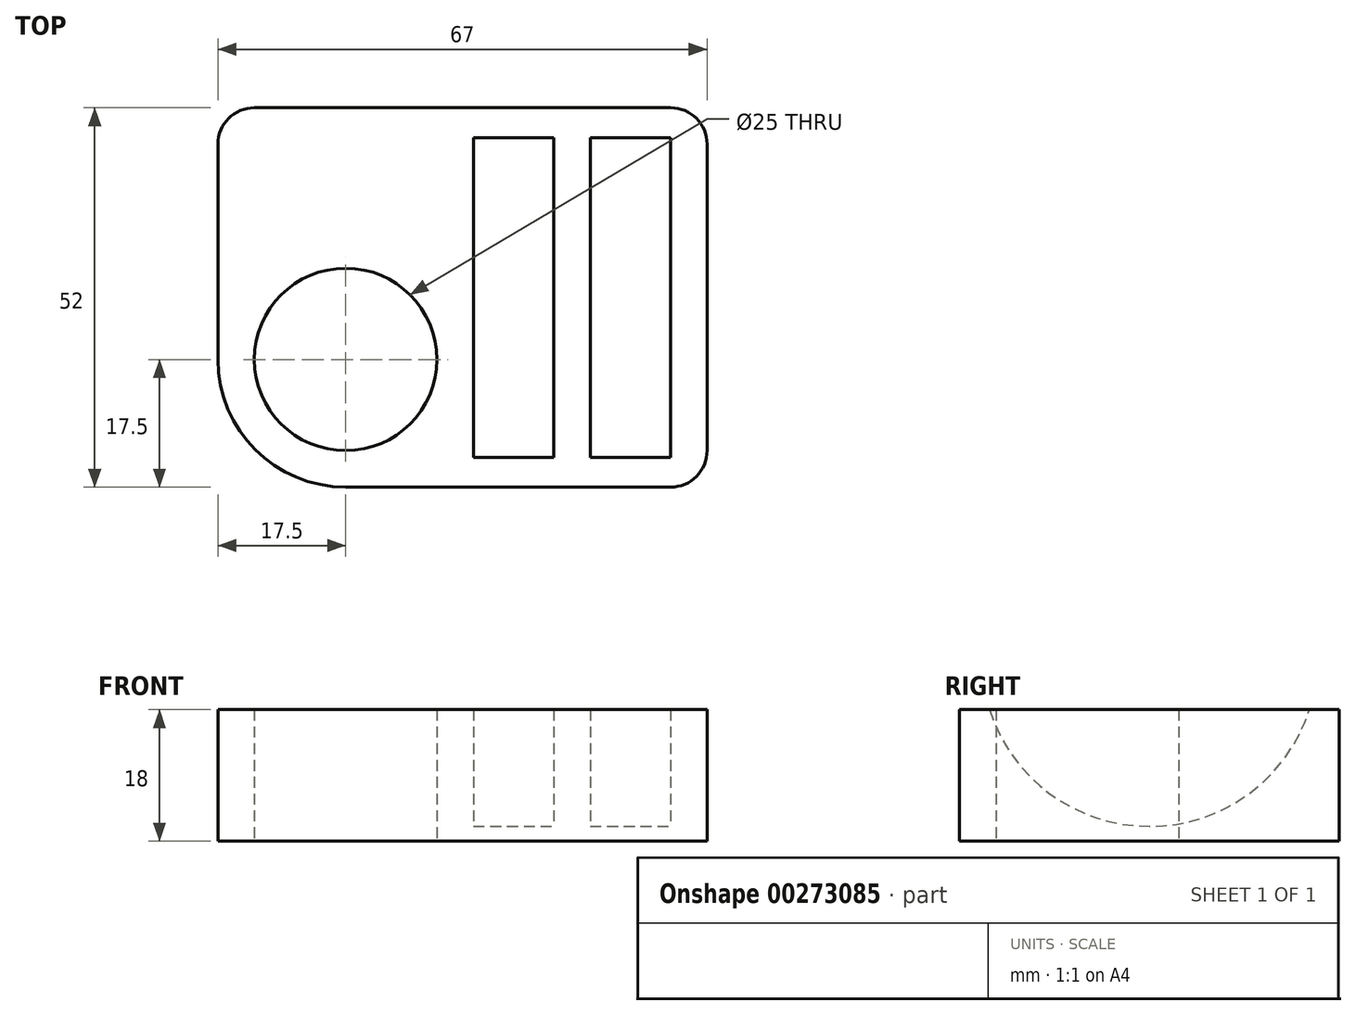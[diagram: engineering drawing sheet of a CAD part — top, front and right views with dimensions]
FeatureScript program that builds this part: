
annotation { "Feature Type Name" : "Feature", "Feature Type Description" : "" }
export const myFeature = defineFeature(function(context is Context, id is Id, definition is map)
    precondition{}
    {
        {
            var Q0;
            Q0=qCreatedBy(makeId("Top.planeOp"),FACE);
            var sketch = newSketch(context, id + "F0", { "sketchPlane" : qUnion([Q0])});
            skLineSegment(sketch, "E0.bottom", {"start": v(17.5, 0) * mm, "end": v(62, 0) * mm});
            skLineSegment(sketch, "E0.top", {"start": v(5, 52) * mm, "end": v(62, 52) * mm});
            skLineSegment(sketch, "E0.left", {"start": v(0, 17.5) * mm, "end": v(0, 47) * mm});
            skLineSegment(sketch, "E0.right", {"start": v(67, 5) * mm, "end": v(67, 47) * mm});
            skLineSegment(sketch, "E1.bottom", {"start": v(0, 0) * mm, "end": v(17.5, 0) * mm, "construction": true});
            skLineSegment(sketch, "E1.top", {"start": v(0, 17.5) * mm, "end": v(17.5, 17.5) * mm, "construction": true});
            skLineSegment(sketch, "E1.left", {"start": v(0, 0) * mm, "end": v(0, 17.5) * mm, "construction": true});
            skLineSegment(sketch, "E1.right", {"start": v(17.5, 0) * mm, "end": v(17.5, 17.5) * mm, "construction": true});
            skCircle(sketch, "E2", {"center": v(17.5, 17.5) * mm, "radius": 12.5 * mm});
            skPoint(sketch, "E3.visualSharp", {"position": v(0, 0) * mm});
            skArc(sketch, "E3.filletArc", {"start": v(0, 17.5) * mm, "mid": v(5.13, 5.13) * mm, "end": v(17.5, 0) * mm});
            skPoint(sketch, "E4.visualSharp", {"position": v(0, 52) * mm});
            skArc(sketch, "E4.filletArc", {"start": v(5, 52) * mm, "mid": v(1.46, 50.54) * mm, "end": v(0, 47) * mm});
            skPoint(sketch, "E5.visualSharp", {"position": v(67, 52) * mm});
            skArc(sketch, "E5.filletArc", {"start": v(67, 47) * mm, "mid": v(65.54, 50.54) * mm, "end": v(62, 52) * mm});
            skPoint(sketch, "E6.visualSharp", {"position": v(67, 0) * mm});
            skArc(sketch, "E6.filletArc", {"start": v(62, 0) * mm, "mid": v(65.54, 1.46) * mm, "end": v(67, 5) * mm});
            skSolve(sketch);
        }
        {
            var Q0;
            Q0=makeQuery(id+"F0.imprint","IMPRINT",FACE,{"disambiguationData":[TD([[makeQuery(id+"F0.imprint","IMPRINT",EDGE,{"derivedFrom":sQuery(id+"F0.wireOp",EDGE,"E0.bottom")}),1.0]])]});
            extrude(context, id + "F1", {"entities" : qUnion([Q0]), "depth" : 25 * mm});
        }
        {
            var Q0;
            Q0=makeQuery(id+"F1.opExtrude","CAP_FACE",FACE,{"disambiguationData":[OSD([sQuery(id+"F0.wireOp",EDGE,"E0.bottom"),sQuery(id+"F0.wireOp",EDGE,"E0.top"),sQuery(id+"F0.wireOp",EDGE,"E0.right"),sQuery(id+"F0.wireOp",EDGE,"E2"),sQuery(id+"F0.wireOp",EDGE,"E3.filletArc"),sQuery(id+"F0.wireOp",EDGE,"E4.filletArc"),sQuery(id+"F0.wireOp",EDGE,"E5.filletArc"),sQuery(id+"F0.wireOp",EDGE,"E6.filletArc")])],"isStart":false});
            var sketch = newSketch(context, id + "F2", { "sketchPlane" : qUnion([Q0])});
            skLineSegment(sketch, "E7.bottom", {"start": v(0, 0) * mm, "end": v(35, 0) * mm, "construction": true});
            skLineSegment(sketch, "E7.top", {"start": v(0, 26) * mm, "end": v(35, 26) * mm, "construction": true});
            skLineSegment(sketch, "E7.left", {"start": v(0, 0) * mm, "end": v(0, 26) * mm, "construction": true});
            skLineSegment(sketch, "E7.right", {"start": v(35, 0) * mm, "end": v(35, 26) * mm, "construction": true});
            skLineSegment(sketch, "E8.bottom", {"start": v(35, 26) * mm, "end": v(46, 26) * mm});
            skLineSegment(sketch, "E8.top", {"start": v(35, 3) * mm, "end": v(46, 3) * mm});
            skLineSegment(sketch, "E8.left", {"start": v(35, 26) * mm, "end": v(35, 3) * mm});
            skLineSegment(sketch, "E8.right", {"start": v(46, 26) * mm, "end": v(46, 3) * mm});
            skLineSegment(sketch, "E9", {"start": v(46, 26) * mm, "end": v(51, 26) * mm, "construction": true});
            skLineSegment(sketch, "E10.bottom", {"start": v(51, 26) * mm, "end": v(62, 26) * mm});
            skLineSegment(sketch, "E10.top", {"start": v(51, 3) * mm, "end": v(62, 3) * mm});
            skLineSegment(sketch, "E10.left", {"start": v(51, 26) * mm, "end": v(51, 3) * mm});
            skLineSegment(sketch, "E10.right", {"start": v(62, 26) * mm, "end": v(62, 3) * mm});
            skSolve(sketch);
        }
        {
            var Q0;
            Q0=makeQuery(id+"F2.imprint","IMPRINT",FACE,{"disambiguationData":[TD([[makeQuery(id+"F2.imprint","IMPRINT",EDGE,{"derivedFrom":sQuery(id+"F2.wireOp",EDGE,"E8.bottom")}),-1.0]])]});
            var Q1;
            Q1=makeQuery(id+"F2.imprint","IMPRINT",FACE,{"disambiguationData":[TD([[makeQuery(id+"F2.imprint","IMPRINT",EDGE,{"derivedFrom":sQuery(id+"F2.wireOp",EDGE,"E10.bottom")}),-1.0]])]});
            var Q2;
            Q2=sQuery(id+"F2.wireOp",EDGE,"E8.bottom");
            revolve(context, id + "F3", {"operationType" : NewBodyOperationType.REMOVE, "entities" : qUnion([Q0, Q1]), "axis" : qUnion([Q2]), "revolveType" : RevolveType.FULL, "oppositeDirection" : true});
        }
        {
            var Q0;
            Q0=makeQuery(id+"F1.opExtrude","SWEPT_FACE",FACE,{"disambiguationData":[OSD([sQuery(id+"F0.wireOp",EDGE,"E0.bottom")])]});
            var sketch = newSketch(context, id + "F4", { "sketchPlane" : qUnion([Q0])});
            skLineSegment(sketch, "E11", {"start": v(0, 0) * mm, "end": v(0, 18) * mm, "construction": true});
            skLineSegment(sketch, "E12.bottom", {"start": v(0, 18) * mm, "end": v(82.21, 18) * mm});
            skLineSegment(sketch, "E12.top", {"start": v(0, 36.05) * mm, "end": v(82.21, 36.05) * mm});
            skLineSegment(sketch, "E12.left", {"start": v(0, 18) * mm, "end": v(0, 36.05) * mm});
            skLineSegment(sketch, "E12.right", {"start": v(82.21, 18) * mm, "end": v(82.21, 36.05) * mm});
            skSolve(sketch);
        }
        {
            var Q0;
            Q0=qSketchRegion(id+"F4",true);
            extrude(context, id + "F5", {"entities" : qUnion([Q0]), "operationType" : NewBodyOperationType.REMOVE, "endBound" : BoundingType.THROUGH_ALL, "oppositeDirection" : true, "depth" : 25 * mm});
        }
    });
